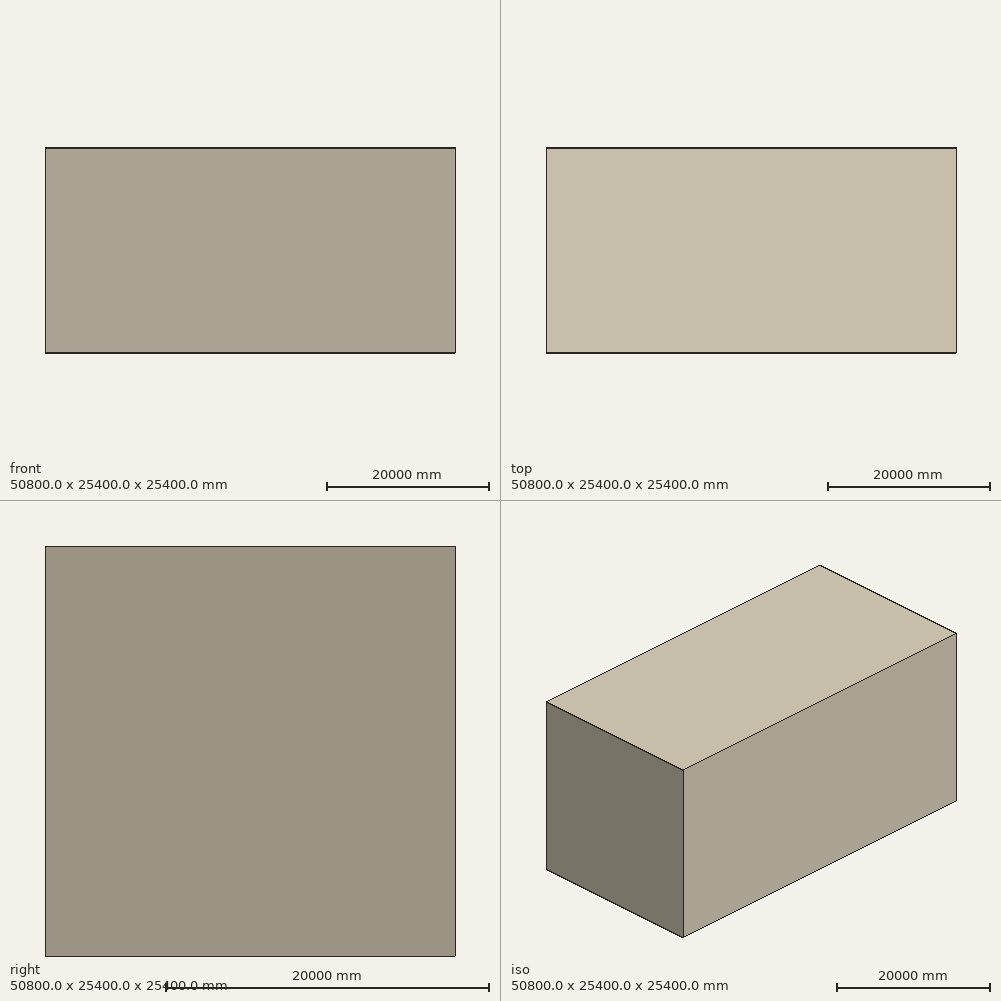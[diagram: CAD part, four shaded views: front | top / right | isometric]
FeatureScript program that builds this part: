
annotation { "Feature Type Name" : "Feature", "Feature Type Description" : "" }
export const myFeature = defineFeature(function(context is Context, id is Id, definition is map)
    precondition{}
    {
        {
            var Q0;
            Q0=qCreatedBy(makeId("Front.planeOp"),FACE);
            var sketch = newSketch(context, id + "F0", { "sketchPlane" : qUnion([Q0])});
            skLineSegment(sketch, "E0", {"start": v(0, 0) * mm, "end": v(-50800, 0) * mm});
            skLineSegment(sketch, "E1", {"start": v(-50800, 0) * mm, "end": v(-50800, 25400) * mm});
            skLineSegment(sketch, "E2", {"start": v(-50800, 25400) * mm, "end": v(0, 25400) * mm});
            skLineSegment(sketch, "E3", {"start": v(0, 25400) * mm, "end": v(0, 0) * mm});
            skSolve(sketch);
        }
        {
            var Q0;
            Q0 = qSketchRegion(id + "F0", true);
            extrude(context, id + "F1", {"entities" : qUnion([Q0]), "depth" : 25400 * mm});
        }
        {
            var Q0;
            Q0=makeQuery(id+"F1.opExtrude","SWEPT_FACE",FACE,{"disambiguationData":[OSD([sQuery(id+"F0.wireOp",EDGE,"E2")])]});
            var Q1;
            Q1=makeQuery(id+"F1.opExtrude","CAP_FACE",FACE,{"disambiguationData":[OSD([sQuery(id+"F0.wireOp",EDGE,"E0"),sQuery(id+"F0.wireOp",EDGE,"E1"),sQuery(id+"F0.wireOp",EDGE,"E2"),sQuery(id+"F0.wireOp",EDGE,"E3")])],"isStart":false});
            fillet(context, id + "F2", {"entities" : qUnion([Q0, Q1]), "radius" : 5.08 * mm, "tangentPropagation" : true, "allowEdgeOverflow" : false});
        }
        {
            var Q0;
            Q0=makeQuery(id+"F1.opExtrude","CAP_FACE",FACE,{"disambiguationData":[OSD([sQuery(id+"F0.wireOp",EDGE,"E0"),sQuery(id+"F0.wireOp",EDGE,"E1"),sQuery(id+"F0.wireOp",EDGE,"E2"),sQuery(id+"F0.wireOp",EDGE,"E3")])],"isStart":false});
            var Q1;
            Q1=makeQuery(id+"F1.opExtrude","SWEPT_FACE",FACE,{"disambiguationData":[OSD([sQuery(id+"F0.wireOp",EDGE,"E0")])]});
            fillet(context, id + "F3", {"entities" : qUnion([Q0, Q1]), "radius" : 5.08 * mm, "tangentPropagation" : true, "allowEdgeOverflow" : false});
        }
    });
